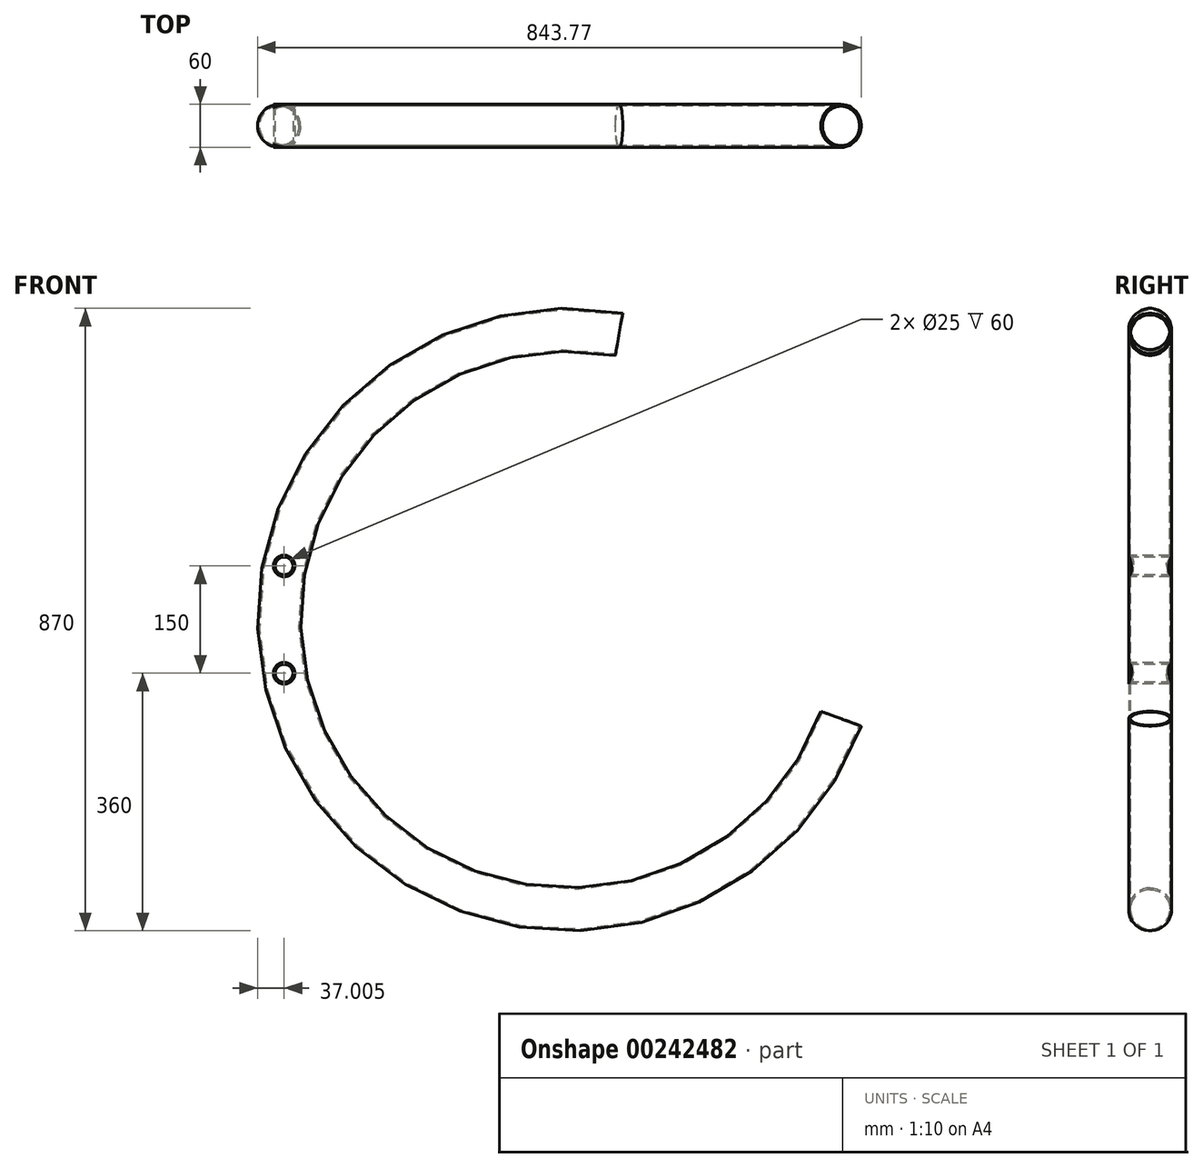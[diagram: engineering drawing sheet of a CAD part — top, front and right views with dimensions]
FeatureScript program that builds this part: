
annotation { "Feature Type Name" : "Feature", "Feature Type Description" : "" }
export const myFeature = defineFeature(function(context is Context, id is Id, definition is map)
    precondition{}
    {
        {
            var Q0;
            Q0=qCreatedBy(makeId("Right.planeOp"),FACE);
            var sketch = newSketch(context, id + "F0", { "sketchPlane" : qUnion([Q0])});
            skLineSegment(sketch, "E0.bottom", {"start": v(0, 0) * mm, "end": v(60, 0) * mm});
            skLineSegment(sketch, "E0.top", {"start": v(0, 60) * mm, "end": v(60, 60) * mm});
            skLineSegment(sketch, "E0.left", {"start": v(0, 0) * mm, "end": v(0, 60) * mm});
            skLineSegment(sketch, "E0.right", {"start": v(60, 0) * mm, "end": v(60, 60) * mm});
            skLineSegment(sketch, "E1", {"start": v(72.51, -375) * mm, "end": v(0, -375) * mm});
            skLineSegment(sketch, "E2.bottom", {"start": v(57.6, 2.4) * mm, "end": v(2.4, 2.4) * mm});
            skLineSegment(sketch, "E2.top", {"start": v(57.6, 57.6) * mm, "end": v(2.4, 57.6) * mm});
            skLineSegment(sketch, "E2.left", {"start": v(57.6, 2.4) * mm, "end": v(57.6, 57.6) * mm});
            skLineSegment(sketch, "E2.right", {"start": v(2.4, 2.4) * mm, "end": v(2.4, 57.6) * mm});
            skSolve(sketch);
        }
        {
            var Q0;
            Q0 = qSketchRegion(id + "F0", true);
            var Q1;
            Q1=sQuery(id+"F0.wireOp",EDGE,"E1");
            revolve(context, id + "F1", {"entities" : qUnion([Q0]), "axis" : qUnion([Q1]), "revolveType" : RevolveType.ONE_DIRECTION, "angle" : 250 * degree});
        }
        {
            var Q0;
            Q0=makeQuery(id+"F1.opRevolve","SWEPT_EDGE",EDGE,{"disambiguationData":[OSD([sQuery(id+"F0.wireOp",EDGE,"E2.top"),sQuery(id+"F0.wireOp",EDGE,"E2.right")])]});
            fillet(context, id + "F2", {"entities" : qUnion([Q0]), "radius" : 27.6 * mm, "tangentPropagation" : true, "allowEdgeOverflow" : false});
        }
        {
            var Q0;
            Q0=makeQuery(id+"F1.opRevolve","SWEPT_EDGE",EDGE,{"disambiguationData":[OSD([sQuery(id+"F0.wireOp",EDGE,"E2.bottom"),sQuery(id+"F0.wireOp",EDGE,"E2.right")])]});
            fillet(context, id + "F3", {"entities" : qUnion([Q0]), "radius" : 27.6 * mm, "tangentPropagation" : true, "allowEdgeOverflow" : false});
        }
        {
            var Q0;
            Q0=makeQuery(id+"F1.opRevolve","SWEPT_EDGE",EDGE,{"disambiguationData":[OSD([sQuery(id+"F0.wireOp",EDGE,"E2.top"),sQuery(id+"F0.wireOp",EDGE,"E2.left")])]});
            fillet(context, id + "F4", {"entities" : qUnion([Q0]), "radius" : 27.6 * mm, "tangentPropagation" : true, "allowEdgeOverflow" : false});
        }
        {
            var Q0;
            Q0=makeQuery(id+"F1.opRevolve","SWEPT_EDGE",EDGE,{"disambiguationData":[OSD([sQuery(id+"F0.wireOp",EDGE,"E2.bottom"),sQuery(id+"F0.wireOp",EDGE,"E2.left")])]});
            fillet(context, id + "F5", {"entities" : qUnion([Q0]), "radius" : 27.6 * mm, "tangentPropagation" : true, "allowEdgeOverflow" : false});
        }
        {
            var Q0;
            Q0=makeQuery(id+"F1.opRevolve","SWEPT_EDGE",EDGE,{"disambiguationData":[OSD([sQuery(id+"F0.wireOp",EDGE,"E0.bottom"),sQuery(id+"F0.wireOp",EDGE,"E0.left")])]});
            fillet(context, id + "F6", {"entities" : qUnion([Q0]), "radius" : 30 * mm, "tangentPropagation" : true, "allowEdgeOverflow" : false});
        }
        {
            var Q0;
            Q0=makeQuery(id+"F1.opRevolve","SWEPT_EDGE",EDGE,{"disambiguationData":[OSD([sQuery(id+"F0.wireOp",EDGE,"E0.bottom"),sQuery(id+"F0.wireOp",EDGE,"E0.right")])]});
            var Q1;
            Q1=makeQuery(id+"F1.opRevolve","SWEPT_EDGE",EDGE,{"disambiguationData":[OSD([sQuery(id+"F0.wireOp",EDGE,"E0.top"),sQuery(id+"F0.wireOp",EDGE,"E0.right")])]});
            var Q2;
            Q2=makeQuery(id+"F1.opRevolve","SWEPT_EDGE",EDGE,{"disambiguationData":[OSD([sQuery(id+"F0.wireOp",EDGE,"E0.top"),sQuery(id+"F0.wireOp",EDGE,"E0.left")])]});
            fillet(context, id + "F7", {"entities" : qUnion([Q0, Q1, Q2]), "radius" : 30 * mm, "tangentPropagation" : true, "allowEdgeOverflow" : false});
        }
        {
            var Q0;
            Q0=makeQuery(id+"F1.opRevolve","CAP_FACE",FACE,{"disambiguationData":[OSD([sQuery(id+"F0.wireOp",EDGE,"E0.bottom"),sQuery(id+"F0.wireOp",EDGE,"E0.top"),sQuery(id+"F0.wireOp",EDGE,"E0.left"),sQuery(id+"F0.wireOp",EDGE,"E0.right"),sQuery(id+"F0.wireOp",EDGE,"E2.bottom"),sQuery(id+"F0.wireOp",EDGE,"E2.top"),sQuery(id+"F0.wireOp",EDGE,"E2.left"),sQuery(id+"F0.wireOp",EDGE,"E2.right")])],"isStart":true});
            var sketch = newSketch(context, id + "F8", { "sketchPlane" : qUnion([Q0])});
            skCircle(sketch, "E3", {"center": v(30, 30) * mm, "radius": 27.6 * mm});
            skCircle(sketch, "E4", {"center": v(30, 30) * mm, "radius": 30 * mm});
            skLineSegment(sketch, "E5", {"start": v(0, -375) * mm, "end": v(71.62, -375) * mm});
            skSolve(sketch);
        }
        {
            var Q0;
            {var subQ0=sQuery(id+"F8.wireOp",EDGE,"E3");var subQ2=makeQuery(id+"F8.imprint","IMPRINT",VERTEX,{"disambiguationData":[OD(2.0)],"derivedFrom":subQ0});Q0=makeQuery(id+"F8.imprint","IMPRINT",FACE,{"disambiguationData":[TD([[makeQuery(id+"F8.imprint","IMPRINT",EDGE,{"disambiguationData":[TD([[subQ2,1.0]])],"derivedFrom":subQ0}),1.0]])]});}
            var Q1;
            Q1=sQuery(id+"F8.wireOp",EDGE,"E5");
            revolve(context, id + "F9", {"operationType" : NewBodyOperationType.ADD, "entities" : qUnion([Q0]), "axis" : qUnion([Q1]), "revolveType" : RevolveType.ONE_DIRECTION, "angle" : 10 * degree});
        }
        {
            var Q0;
            Q0=qCreatedBy(makeId("Front.planeOp"),FACE);
            var sketch = newSketch(context, id + "F10", { "sketchPlane" : qUnion([Q0])});
            skArc(sketch, "E6", {"start": v(65.12, -5.7) * mm, "mid": v(-324.76, -562.5) * mm, "end": v(352.38, -503.26) * mm});
            skArc(sketch, "E7", {"start": v(75.54, 53.4) * mm, "mid": v(-376.72, -592.5) * mm, "end": v(408.77, -523.78) * mm});
            skCircle(sketch, "E8", {"center": v(-398, -450) * mm, "radius": 15 * mm});
            skCircle(sketch, "E9", {"center": v(-398, -300) * mm, "radius": 15 * mm});
            skSolve(sketch);
        }
        {
            var Q0;
            Q0=makeQuery(id+"F10.imprint","IMPRINT",FACE,{"disambiguationData":[TD([[makeQuery(id+"F10.imprint","IMPRINT",EDGE,{"derivedFrom":sQuery(id+"F10.wireOp",EDGE,"E9")}),1.0]])]});
            var Q1;
            Q1=makeQuery(id+"F10.imprint","IMPRINT",FACE,{"disambiguationData":[TD([[makeQuery(id+"F10.imprint","IMPRINT",EDGE,{"derivedFrom":sQuery(id+"F10.wireOp",EDGE,"E8")}),1.0]])]});
            extrude(context, id + "F11", {"entities" : qUnion([Q0, Q1]), "operationType" : NewBodyOperationType.REMOVE, "oppositeDirection" : true, "depth" : 70 * mm});
        }
        {
            var Q0;
            Q0=qCreatedBy(makeId("Front.planeOp"),FACE);
            var sketch = newSketch(context, id + "F12", { "sketchPlane" : qUnion([Q0])});
            skCircle(sketch, "E10.0", {"center": v(-398, -300) * mm, "radius": 15 * mm});
            skCircle(sketch, "E11", {"center": v(-398, -300) * mm, "radius": 12.5 * mm});
            skCircle(sketch, "E12.0", {"center": v(-398, -450) * mm, "radius": 15 * mm});
            skCircle(sketch, "E13", {"center": v(-398, -450) * mm, "radius": 12.5 * mm});
            skSolve(sketch);
        }
        {
            var Q0;
            Q0=makeQuery(id+"F12.imprint","IMPRINT",FACE,{"disambiguationData":[TD([[makeQuery(id+"F12.imprint","IMPRINT",EDGE,{"derivedFrom":sQuery(id+"F12.wireOp",EDGE,"E13")}),-1.0]])]});
            var Q1;
            Q1=makeQuery(id+"F12.imprint","IMPRINT",FACE,{"disambiguationData":[TD([[makeQuery(id+"F12.imprint","IMPRINT",EDGE,{"derivedFrom":sQuery(id+"F12.wireOp",EDGE,"E10.0")}),1.0]])]});
            extrude(context, id + "F13", {"entities" : qUnion([Q0, Q1]), "operationType" : NewBodyOperationType.ADD, "oppositeDirection" : true, "depth" : 60 * mm});
        }
    });
